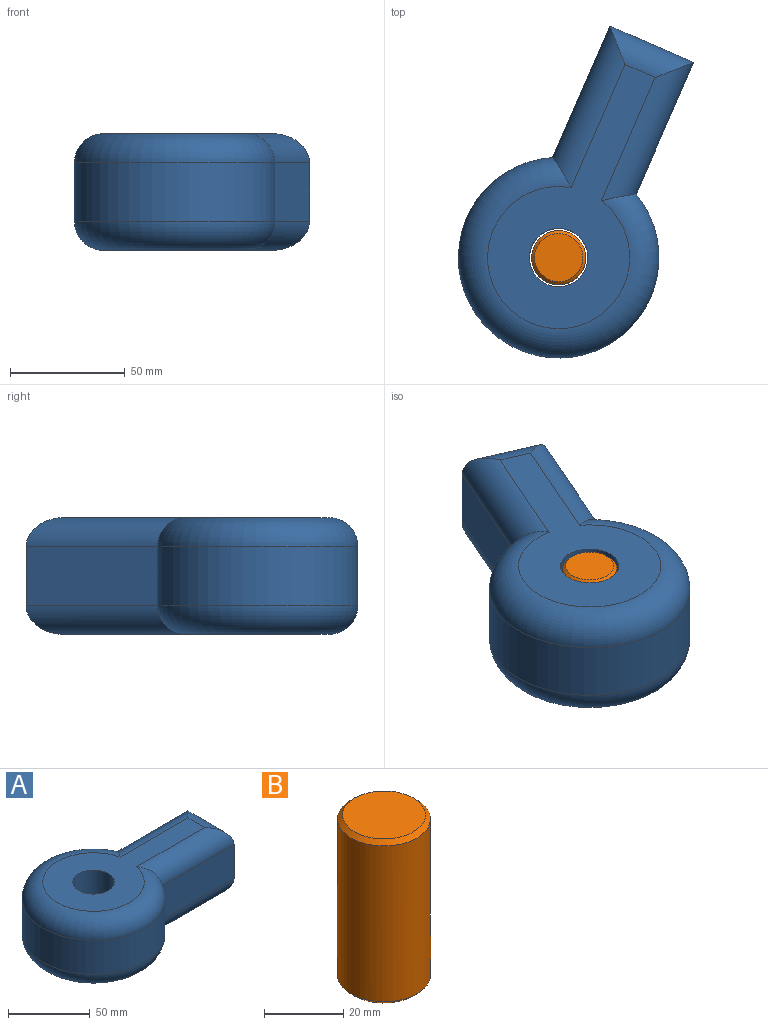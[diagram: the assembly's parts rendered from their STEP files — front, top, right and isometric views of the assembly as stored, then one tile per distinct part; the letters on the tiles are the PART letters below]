
ASSEMBLY  parts=2 mates=1
PART A: 15 faces, bbox 148.5x94.4x50.8 mm
  f0: plane 62.45x25.4mm, normal (0,1,0), area 1586.1mm2, adj f1,f3,f6,f10
  f1: cylinder r=43.62mm len=87.24mm, axis (0,0,-1), area 5913.3mm2, adj f0,f2,f7,f11
  f2: plane 62.45x25.4mm, normal (0,-1,0), area 1586.1mm2, adj f1,f3,f9,f13
  f3: plane 39.75x25.4mm, normal (1,0,0), area 1009.6mm2, adj f0,f2,f8,f12
  f4: plane 119.5x61.84mm, normal (0,0,1), area 3328.2mm2, adj f10,f11,f12,f13,f14
  f5: plane 119.5x61.84mm, normal (0,0,-1), area 3328.2mm2, adj f6,f7,f8,f9,f14
  f6: cylinder r=12.7mm len=71.2mm, axis (-1,0,0), area 1214.2mm2, adj f0,f5,f7,f8
  f7: torus R=30.92mm, axis (0,0,1), area 4262.2mm2, adj f1,f5,f6,f9
  f8: cylinder r=12.7mm len=39.75mm, axis (0,1,0), area 608.8mm2, adj f3,f5,f6,f9
  f9: cylinder r=12.7mm len=71.2mm, axis (1,0,0), area 1214.2mm2, adj f2,f5,f7,f8
  f10: cylinder r=12.7mm len=71.2mm, axis (1,0,0), area 1214.2mm2, adj f0,f4,f11,f12
  f11: torus R=30.92mm, axis (0,0,1), area 4262.2mm2, adj f1,f4,f10,f13
  f12: cylinder r=12.7mm len=39.75mm, axis (0,-1,0), area 608.8mm2, adj f3,f4,f10,f13
  f13: cylinder r=12.7mm len=71.2mm, axis (-1,0,0), area 1214.2mm2, adj f2,f4,f11,f12
  f14: cylinder r=12.7mm len=50.8mm, axis (0,0,-1), area 4053.7mm2, adj f4,f5
PART B: 5 faces, bbox 23.5x23.5x50.8 mm
  f0: plane 20.99x20.99mm, normal (0,0,1), area 346mm2, adj f3
  f1: plane 20.99x20.99mm, normal (0,0,-1), area 346mm2, adj f4
  f2: cylinder r=11.77mm len=48.26mm, axis (0,0,-1), area 3567.5mm2, adj f3,f4
  f3: cone r=11.77mm half-angle=45deg, axis (0,0,-1), area 125.6mm2, adj f0,f2
  f4: cone r=10.5mm half-angle=45deg, axis (0,0,1), area 125.6mm2, adj f1,f2
PLACE A rot(axis=(0,0,1),66.4deg) t=(-20.12,51.03,50.28)mm
PLACE B t=(51.28,-18.24,50.28)mm fixed
MATE revolute A.f14 <-> B.f2  axis (0,0,1) through (-37.3,-38.11,0.54)mm
